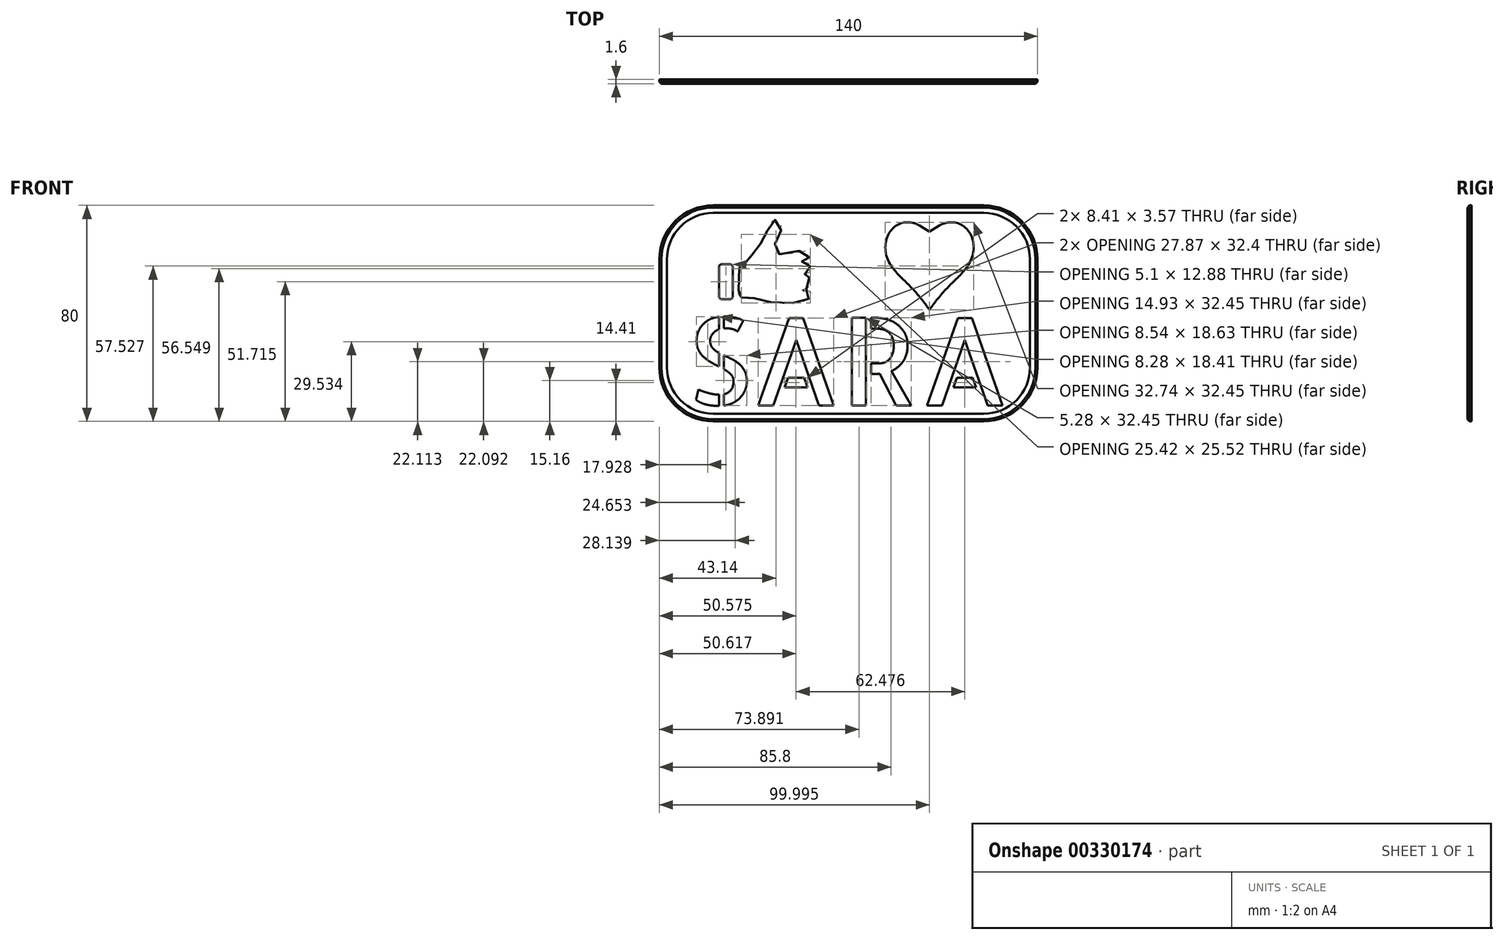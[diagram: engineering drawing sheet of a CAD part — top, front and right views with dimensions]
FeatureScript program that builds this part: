
annotation { "Feature Type Name" : "Feature", "Feature Type Description" : "" }
export const myFeature = defineFeature(function(context is Context, id is Id, definition is map)
    precondition{}
    {
        {
            var Q0;
            Q0=qCreatedBy(makeId("Front.planeOp"),FACE);
            var sketch = newSketch(context, id + "F0", { "sketchPlane" : qUnion([Q0])});
            skLineSegment(sketch, "E0.bottom", {"start": v(-70, 60) * mm, "end": v(70, 60) * mm});
            skLineSegment(sketch, "E0.top", {"start": v(-70, -20) * mm, "end": v(70, -20) * mm});
            skLineSegment(sketch, "E0.left", {"start": v(-70, 60) * mm, "end": v(-70, -20) * mm});
            skLineSegment(sketch, "E0.right", {"start": v(70, 60) * mm, "end": v(70, -20) * mm});
            skSolve(sketch);
        }
        {
            var Q0;
            Q0=qSketchRegion(id+"F0",true);
            extrude(context, id + "F1", {"entities" : qUnion([Q0]), "depth" : 1.6 * mm});
        }
        {
            var Q0;
            Q0=makeQuery(id+"F1.opExtrude","CAP_FACE",FACE,{"disambiguationData":[OSD([sQuery(id+"F0.wireOp",EDGE,"E0.bottom"),sQuery(id+"F0.wireOp",EDGE,"E0.top"),sQuery(id+"F0.wireOp",EDGE,"E0.left"),sQuery(id+"F0.wireOp",EDGE,"E0.right")])],"isStart":false});
            var sketch = newSketch(context, id + "F2", { "sketchPlane" : qUnion([Q0])});
            skText(sketch, "E1", { "text": "SARA", "fontName": "AllertaStencil-Regular.ttf"});
            skText(sketch, "E2", { "text": "♥", "fontName": "NotoSansCJKjp-Regular.otf"});
            const initialGuessF2  = {"E1": [-0.06, -0.01411, 1, 0, 0.03246], "E2": [0.01055, 0.0228, 1, 0, 0.028]};
            skSetInitialGuess(sketch, initialGuessF2);
            skSolve(sketch);
        }
        {
            var Q0;
            Q0=qSketchRegion(id+"F2",true);
            extrude(context, id + "F3", {"entities" : qUnion([Q0]), "operationType" : NewBodyOperationType.REMOVE, "endBound" : BoundingType.THROUGH_ALL, "oppositeDirection" : true, "depth" : 25 * mm});
        }
        {
            var Q0;
            Q0=makeQuery(id+"F1.opExtrude","SWEPT_EDGE",EDGE,{"disambiguationData":[OSD([sQuery(id+"F0.wireOp",EDGE,"E0.top"),sQuery(id+"F0.wireOp",EDGE,"E0.right")])]});
            var Q1;
            Q1=makeQuery(id+"F1.opExtrude","SWEPT_EDGE",EDGE,{"disambiguationData":[OSD([sQuery(id+"F0.wireOp",EDGE,"E0.bottom"),sQuery(id+"F0.wireOp",EDGE,"E0.right")])]});
            var Q2;
            Q2=makeQuery(id+"F1.opExtrude","SWEPT_EDGE",EDGE,{"disambiguationData":[OSD([sQuery(id+"F0.wireOp",EDGE,"E0.top"),sQuery(id+"F0.wireOp",EDGE,"E0.left")])]});
            var Q3;
            Q3=makeQuery(id+"F1.opExtrude","SWEPT_EDGE",EDGE,{"disambiguationData":[OSD([sQuery(id+"F0.wireOp",EDGE,"E0.bottom"),sQuery(id+"F0.wireOp",EDGE,"E0.left")])]});
            fillet(context, id + "F4", {"entities" : qUnion([Q0, Q1, Q2, Q3]), "radius" : 20 * mm, "tangentPropagation" : true, "allowEdgeOverflow" : false});
        }
        {
            var Q0;
            Q0=makeQuery(id+"F1.opExtrude","CAP_EDGE",EDGE,{"disambiguationData":[OSD([sQuery(id+"F0.wireOp",EDGE,"E0.top")])],"isStart":false});
            chamfer(context, id + "F5", {"entities" : qUnion([Q0]), "width" : 0.8 * mm, "tangentPropagation" : true});
        }
        {
            var Q0;
            Q0=makeQuery(id+"F1.opExtrude","CAP_FACE",FACE,{"disambiguationData":[OSD([sQuery(id+"F0.wireOp",EDGE,"E0.bottom"),sQuery(id+"F0.wireOp",EDGE,"E0.top"),sQuery(id+"F0.wireOp",EDGE,"E0.left"),sQuery(id+"F0.wireOp",EDGE,"E0.right")])],"isStart":false});
            var sketch = newSketch(context, id + "F6", { "sketchPlane" : qUnion([Q0])});
            skLineSegment(sketch, "E3.0", {"start": v(-50, -17.2) * mm, "end": v(50, -17.2) * mm});
            skArc(sketch, "E3.1", {"start": v(-67.2, 0) * mm, "mid": v(-62.16, -12.16) * mm, "end": v(-50, -17.2) * mm});
            skArc(sketch, "E3.2", {"start": v(50, -17.2) * mm, "mid": v(62.16, -12.16) * mm, "end": v(67.2, 0) * mm});
            skLineSegment(sketch, "E3.3", {"start": v(-67.2, 40) * mm, "end": v(-67.2, 0) * mm});
            skLineSegment(sketch, "E3.4", {"start": v(67.2, 0) * mm, "end": v(67.2, 40) * mm});
            skArc(sketch, "E3.5", {"start": v(67.2, 40) * mm, "mid": v(62.16, 52.16) * mm, "end": v(50, 57.2) * mm});
            skLineSegment(sketch, "E3.6", {"start": v(50, 57.2) * mm, "end": v(-50, 57.2) * mm});
            skArc(sketch, "E3.7", {"start": v(-50, 57.2) * mm, "mid": v(-62.16, 52.16) * mm, "end": v(-67.2, 40) * mm});
            skSolve(sketch);
        }
        {
            var Q0;
            Q0=qSketchRegion(id+"F6",true);
            extrude(context, id + "F7", {"entities" : qUnion([Q0]), "operationType" : NewBodyOperationType.REMOVE, "oppositeDirection" : true, "depth" : 0.4 * mm});
        }
        {
            var Q0;
            Q0=makeQuery(id+"F7.boolean.opBoolean","COPY",FACE,{"derivedFrom":makeQuery(id+"F7.opExtrude","CAP_FACE",FACE,{"disambiguationData":[OSD([sQuery(id+"F6.wireOp",EDGE,"E3.0"),sQuery(id+"F6.wireOp",EDGE,"E3.1"),sQuery(id+"F6.wireOp",EDGE,"E3.2"),sQuery(id+"F6.wireOp",EDGE,"E3.3"),sQuery(id+"F6.wireOp",EDGE,"E3.4"),sQuery(id+"F6.wireOp",EDGE,"E3.5"),sQuery(id+"F6.wireOp",EDGE,"E3.6"),sQuery(id+"F6.wireOp",EDGE,"E3.7")])],"isStart":false})});
            var sketch = newSketch(context, id + "F8", { "sketchPlane" : qUnion([Q0])});
            skLineSegment(sketch, "E4", {"start": v(33.7, 52.55) * mm, "end": v(30, 50.27) * mm});
            skLineSegment(sketch, "E5", {"start": v(30, 50.27) * mm, "end": v(26.26, 52.57) * mm});
            skLineSegment(sketch, "E6", {"start": v(26.26, 52.57) * mm, "end": v(25.84, 44.7) * mm});
            skLineSegment(sketch, "E7", {"start": v(25.84, 44.7) * mm, "end": v(33.66, 44.27) * mm});
            skLineSegment(sketch, "E8", {"start": v(33.66, 44.27) * mm, "end": v(33.7, 52.55) * mm});
            skSolve(sketch);
        }
        {
            var Q0;
            Q0=qSketchRegion(id+"F8",true);
            extrude(context, id + "F9", {"entities" : qUnion([Q0]), "operationType" : NewBodyOperationType.REMOVE, "oppositeDirection" : true, "depth" : 25 * mm});
        }
        {
            var Q0;
            Q0=makeQuery(id+"F7.boolean.opBoolean","COPY",FACE,{"derivedFrom":makeQuery(id+"F7.opExtrude","CAP_FACE",FACE,{"disambiguationData":[OSD([sQuery(id+"F6.wireOp",EDGE,"E3.0"),sQuery(id+"F6.wireOp",EDGE,"E3.1"),sQuery(id+"F6.wireOp",EDGE,"E3.2"),sQuery(id+"F6.wireOp",EDGE,"E3.3"),sQuery(id+"F6.wireOp",EDGE,"E3.4"),sQuery(id+"F6.wireOp",EDGE,"E3.5"),sQuery(id+"F6.wireOp",EDGE,"E3.6"),sQuery(id+"F6.wireOp",EDGE,"E3.7")])],"isStart":false})});
            var sketch = newSketch(context, id + "F10", { "sketchPlane" : qUnion([Q0])});
            skFitSpline(sketch, "E9", {"points": [v(-39.57, 25.93) * mm, v(-40.32, 26.28) * mm, v(-40.6, 27.2) * mm, v(-40.34, 37.25) * mm, v(-40.19, 37.43) * mm, v(-39.33, 37.55) * mm, v(-37.33, 39.73) * mm, v(-35.58, 41.85) * mm, v(-32.38, 46.04) * mm, v(-30.1, 50.4) * mm, v(-27.74, 54.55) * mm, v(-24.91, 52.7) * mm, v(-26.13, 47.63) * mm, v(-27.4, 44) * mm, v(-24.51, 41.68) * mm, v(-15.6, 43.14) * mm, v(-14.8, 40.27) * mm, v(-17.15, 39.55) * mm, v(-17.1, 39.04) * mm, v(-14.65, 38.45) * mm, v(-14.5, 34.98) * mm, v(-16.38, 34.5) * mm, v(-16.38, 34.07) * mm, v(-14.53, 33.32) * mm, v(-14.59, 29.91) * mm, v(-16.51, 28.97) * mm, v(-16.72, 28.5) * mm, v(-14.52, 28.16) * mm, v(-14.39, 25.82) * mm, v(-19.42, 23.95) * mm, v(-30.09, 24.31) * mm, v(-36.28, 25.88) * mm, v(-39.57, 25.93) * mm]});
            skLineSegment(sketch, "E10.bottom", {"start": v(-43.8, 38.15) * mm, "end": v(-46.9, 38.15) * mm});
            skLineSegment(sketch, "E10.top", {"start": v(-43.8, 25.28) * mm, "end": v(-46.9, 25.28) * mm});
            skLineSegment(sketch, "E10.left", {"start": v(-42.8, 37.15) * mm, "end": v(-42.8, 26.28) * mm});
            skLineSegment(sketch, "E10.right", {"start": v(-47.9, 37.15) * mm, "end": v(-47.9, 26.28) * mm});
            skPoint(sketch, "E11.visualSharp", {"position": v(-42.8, 38.15) * mm});
            skArc(sketch, "E11.filletArc", {"start": v(-42.8, 37.15) * mm, "mid": v(-43.1, 37.86) * mm, "end": v(-43.8, 38.15) * mm});
            skPoint(sketch, "E12.visualSharp", {"position": v(-47.9, 38.15) * mm});
            skArc(sketch, "E12.filletArc", {"start": v(-46.9, 38.15) * mm, "mid": v(-47.6, 37.86) * mm, "end": v(-47.9, 37.15) * mm});
            skPoint(sketch, "E13.visualSharp", {"position": v(-47.9, 25.28) * mm});
            skArc(sketch, "E13.filletArc", {"start": v(-47.9, 26.28) * mm, "mid": v(-47.6, 25.57) * mm, "end": v(-46.9, 25.28) * mm});
            skPoint(sketch, "E14.visualSharp", {"position": v(-42.8, 25.28) * mm});
            skArc(sketch, "E14.filletArc", {"start": v(-43.8, 25.28) * mm, "mid": v(-43.1, 25.57) * mm, "end": v(-42.8, 26.28) * mm});
            skSolve(sketch);
        }
        {
            var Q0;
            Q0=qSketchRegion(id+"F10",true);
            extrude(context, id + "F11", {"entities" : qUnion([Q0]), "operationType" : NewBodyOperationType.REMOVE, "endBound" : BoundingType.THROUGH_ALL, "oppositeDirection" : true, "depth" : 25 * mm});
        }
    });
